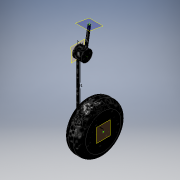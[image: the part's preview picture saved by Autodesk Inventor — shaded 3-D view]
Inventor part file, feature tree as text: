
AUTODESK INVENTOR PART (.ipt)
format: ipt  version: 2018 (Build 220112000, 112)  size: 177,664 bytes
history: native  units: in
note: dims shown in document units (in); Inventor stores cm internally (conversion verified against a paired STEP export)
features: sketch x5, plane x3, extrude x2, sweep x2, fillet x1
ambient origin geometry x8: Origin, YZ Plane, XZ Plane, XY Plane, X Axis, Y Axis, Z Axis, Center Point
bodies: Solid1 (feature_tree), Solid2 (feature_tree)
feature tree (13):
  sketch  "3D Sketch1"
  plane  "Work Plane1"
  extrude  "Extrusion1"  Depth=3.5827in
  plane  "Work Plane2"
  sketch  "Sketch2"  dims[d2=0.4528in d3=0.7047in]
  plane  "Work Plane3"
  sweep  "Sweep1"
  sweep  "Sweep2"
  extrude  "Extrusion2"  TaperAngle=0.0deg  [1 undecoded]
  fillet  "Fillet1"  [1 undecoded]
  sketch  "Sketch1"  dims[d0=1.5866in d1=3.5827in]
  sketch  "Sketch3"  dims[d4=0.5512in d5=0.0in d6=0.1575in]
  sketch  "Sketch4"  dims[d7=0.1575in d8=0.0in d9=0.0in d10=0.0in d11=0.0in d12=3.0in d13=1.063in d14=0.0in d15=0.3937in]
note: 2 required parameter values undecoded (feature->parameter linkage not recoverable at this tier; creation-order binding heuristic only, values carry confidence <= 0.55)
